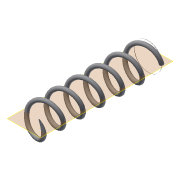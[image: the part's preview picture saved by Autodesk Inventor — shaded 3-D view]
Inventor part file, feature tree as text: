
AUTODESK INVENTOR PART (.ipt)
format: ipt  version: 2016 (Build 200138000, 138)  size: 354,816 bytes
history: native  units: in
note: dims shown in document units (in); Inventor stores cm internally (conversion verified against a paired STEP export)
features: other x1, extrude x1, imported_body x1, sketch x1
ambient origin geometry x8: Origin, YZ Plane, XZ Plane, XY Plane, X Axis, Y Axis, Z Axis, Center Point
bodies: Solid1 (feature_tree)
feature tree (4):
  other  "spring.ipt1"
  extrude  "Extrusion1"  [1 undecoded]
  imported_body  "Base1"
  sketch  "Sketch1"  dims[d0=0.3937in d1=0.0in]
note: 1 required parameter value undecoded (feature->parameter linkage not recoverable at this tier; creation-order binding heuristic only, values carry confidence <= 0.55)
